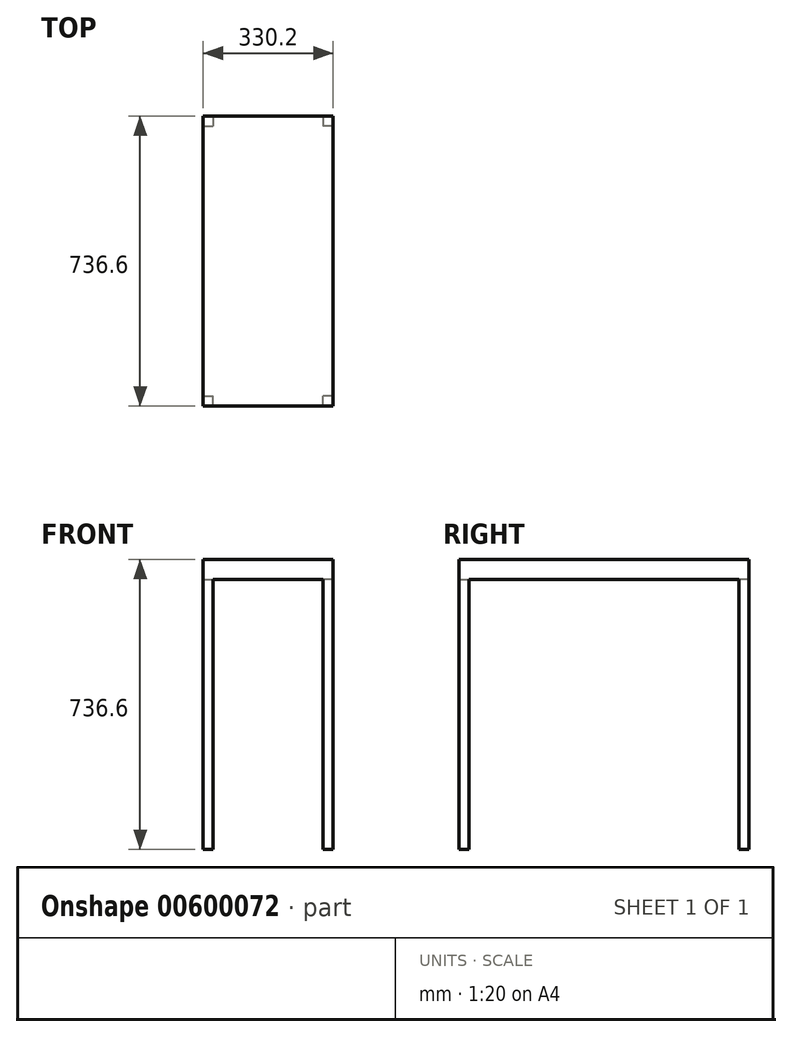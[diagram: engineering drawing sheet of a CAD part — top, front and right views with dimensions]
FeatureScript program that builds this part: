
annotation { "Feature Type Name" : "Feature", "Feature Type Description" : "" }
export const myFeature = defineFeature(function(context is Context, id is Id, definition is map)
    precondition{}
    {
        {
            var Q0;
            Q0=qCreatedBy(makeId("Top.planeOp"),FACE);
            var sketch = newSketch(context, id + "F0", { "sketchPlane" : qUnion([Q0])});
            skLineSegment(sketch, "E0.bottom", {"start": v(165.1, 368.3) * mm, "end": v(-165.1, 368.3) * mm});
            skLineSegment(sketch, "E0.top", {"start": v(165.1, -368.3) * mm, "end": v(-165.1, -368.3) * mm});
            skLineSegment(sketch, "E0.left", {"start": v(165.1, 368.3) * mm, "end": v(165.1, -368.3) * mm});
            skLineSegment(sketch, "E0.right", {"start": v(-165.1, 368.3) * mm, "end": v(-165.1, -368.3) * mm});
            skPoint(sketch, "E0.middle", {"position": v(0, 0) * mm});
            skSolve(sketch);
        }
        {
            var Q0;
            Q0=makeQuery(id+"F0.imprint","IMPRINT",FACE,{"disambiguationData":[TD([[makeQuery(id+"F0.imprint","IMPRINT",EDGE,{"derivedFrom":sQuery(id+"F0.wireOp",EDGE,"E0.bottom")}),1.0]])]});
            extrude(context, id + "F1", {"entities" : qUnion([Q0]), "depth" : 50.8 * mm, "offsetDistance" : 25.4 * mm});
        }
        {
            var Q0;
            Q0=makeQuery(id+"F1.opExtrude","CAP_FACE",FACE,{"disambiguationData":[OSD([sQuery(id+"F0.wireOp",EDGE,"E0.bottom"),sQuery(id+"F0.wireOp",EDGE,"E0.top"),sQuery(id+"F0.wireOp",EDGE,"E0.left"),sQuery(id+"F0.wireOp",EDGE,"E0.right")])],"isStart":true});
            var sketch = newSketch(context, id + "F2", { "sketchPlane" : qUnion([Q0])});
            skLineSegment(sketch, "E1.bottom", {"start": v(-165.1, 368.3) * mm, "end": v(-139.7, 368.3) * mm});
            skLineSegment(sketch, "E1.top", {"start": v(-165.1, 342.9) * mm, "end": v(-139.7, 342.9) * mm});
            skLineSegment(sketch, "E1.left", {"start": v(-165.1, 368.3) * mm, "end": v(-165.1, 342.9) * mm});
            skLineSegment(sketch, "E1.right", {"start": v(-139.7, 368.3) * mm, "end": v(-139.7, 342.9) * mm});
            skLineSegment(sketch, "E2.MirrorCS", {"start": v(139.7, 368.3) * mm, "end": v(139.7, 342.9) * mm});
            skLineSegment(sketch, "E3.MirrorCS", {"start": v(165.1, 368.3) * mm, "end": v(165.1, 342.9) * mm});
            skLineSegment(sketch, "E4.MirrorCS", {"start": v(165.1, 342.9) * mm, "end": v(139.7, 342.9) * mm});
            skLineSegment(sketch, "E5.MirrorCS", {"start": v(165.1, 368.3) * mm, "end": v(139.7, 368.3) * mm});
            skLineSegment(sketch, "E6.MirrorCS", {"start": v(165.1, -368.3) * mm, "end": v(139.7, -368.3) * mm});
            skLineSegment(sketch, "E7.MirrorCS", {"start": v(139.7, -368.3) * mm, "end": v(139.7, -342.9) * mm});
            skLineSegment(sketch, "E8.MirrorCS", {"start": v(165.1, -342.9) * mm, "end": v(139.7, -342.9) * mm});
            skLineSegment(sketch, "E9.MirrorCS", {"start": v(165.1, -368.3) * mm, "end": v(165.1, -342.9) * mm});
            skLineSegment(sketch, "E10.MirrorCS", {"start": v(-165.1, -368.3) * mm, "end": v(-139.7, -368.3) * mm});
            skLineSegment(sketch, "E11.MirrorCS", {"start": v(-165.1, -368.3) * mm, "end": v(-165.1, -342.9) * mm});
            skLineSegment(sketch, "E12.MirrorCS", {"start": v(-165.1, -342.9) * mm, "end": v(-139.7, -342.9) * mm});
            skLineSegment(sketch, "E13.MirrorCS", {"start": v(-139.7, -368.3) * mm, "end": v(-139.7, -342.9) * mm});
            skSolve(sketch);
        }
        {
            var Q0;
            Q0=makeQuery(id+"F2.imprint","IMPRINT",FACE,{"disambiguationData":[TD([[makeQuery(id+"F2.imprint","IMPRINT",EDGE,{"derivedFrom":sQuery(id+"F2.wireOp",EDGE,"E1.bottom")}),1.0]])]});
            var Q1;
            Q1=makeQuery(id+"F2.imprint","IMPRINT",FACE,{"disambiguationData":[TD([[makeQuery(id+"F2.imprint","IMPRINT",EDGE,{"derivedFrom":sQuery(id+"F2.wireOp",EDGE,"E2.MirrorCS")}),1.0]])]});
            var Q2;
            Q2=makeQuery(id+"F2.imprint","IMPRINT",FACE,{"disambiguationData":[TD([[makeQuery(id+"F2.imprint","IMPRINT",EDGE,{"derivedFrom":sQuery(id+"F2.wireOp",EDGE,"E6.MirrorCS")}),-1.0]])]});
            var Q3;
            Q3=makeQuery(id+"F2.imprint","IMPRINT",FACE,{"disambiguationData":[TD([[makeQuery(id+"F2.imprint","IMPRINT",EDGE,{"derivedFrom":sQuery(id+"F2.wireOp",EDGE,"E10.MirrorCS")}),-1.0]])]});
            extrude(context, id + "F3", {"entities" : qUnion([Q0, Q1, Q2, Q3]), "operationType" : NewBodyOperationType.ADD, "depth" : 685.8 * mm, "offsetDistance" : 25.4 * mm});
        }
    });
